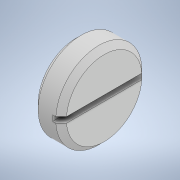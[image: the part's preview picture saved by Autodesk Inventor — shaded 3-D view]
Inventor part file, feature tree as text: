
AUTODESK INVENTOR PART (.ipt)
format: ipt  version: 2022 (Build 260153000, 153)  size: 174,592 bytes
history: native  units: mm
features: sketch x4, other x2, revolve x2, hole x1, extrude x1, thread x1
ambient origin geometry x8: Origin, YZ Plane, XZ Plane, XY Plane, X Axis, Y Axis, Z Axis, Center Point
bodies: Body1 (feature_tree)
feature tree (11):
  other  "Твердое тело1"
  revolve  "Вращение1"
  hole  "Отверстие1"  [1 undecoded]
  revolve  "Вращение2"
  other  "РабПлоскость1"
  extrude  "Выдавливание1"  Depth=4.0mm
  thread  "Резьба1"
  sketch  "Эскиз1"
  sketch  "Эскиз2"
  sketch  "Эскиз3"
  sketch  "Эскиз4"
note: 1 required parameter value undecoded (feature->parameter linkage not recoverable at this tier; creation-order binding heuristic only, values carry confidence <= 0.55)
